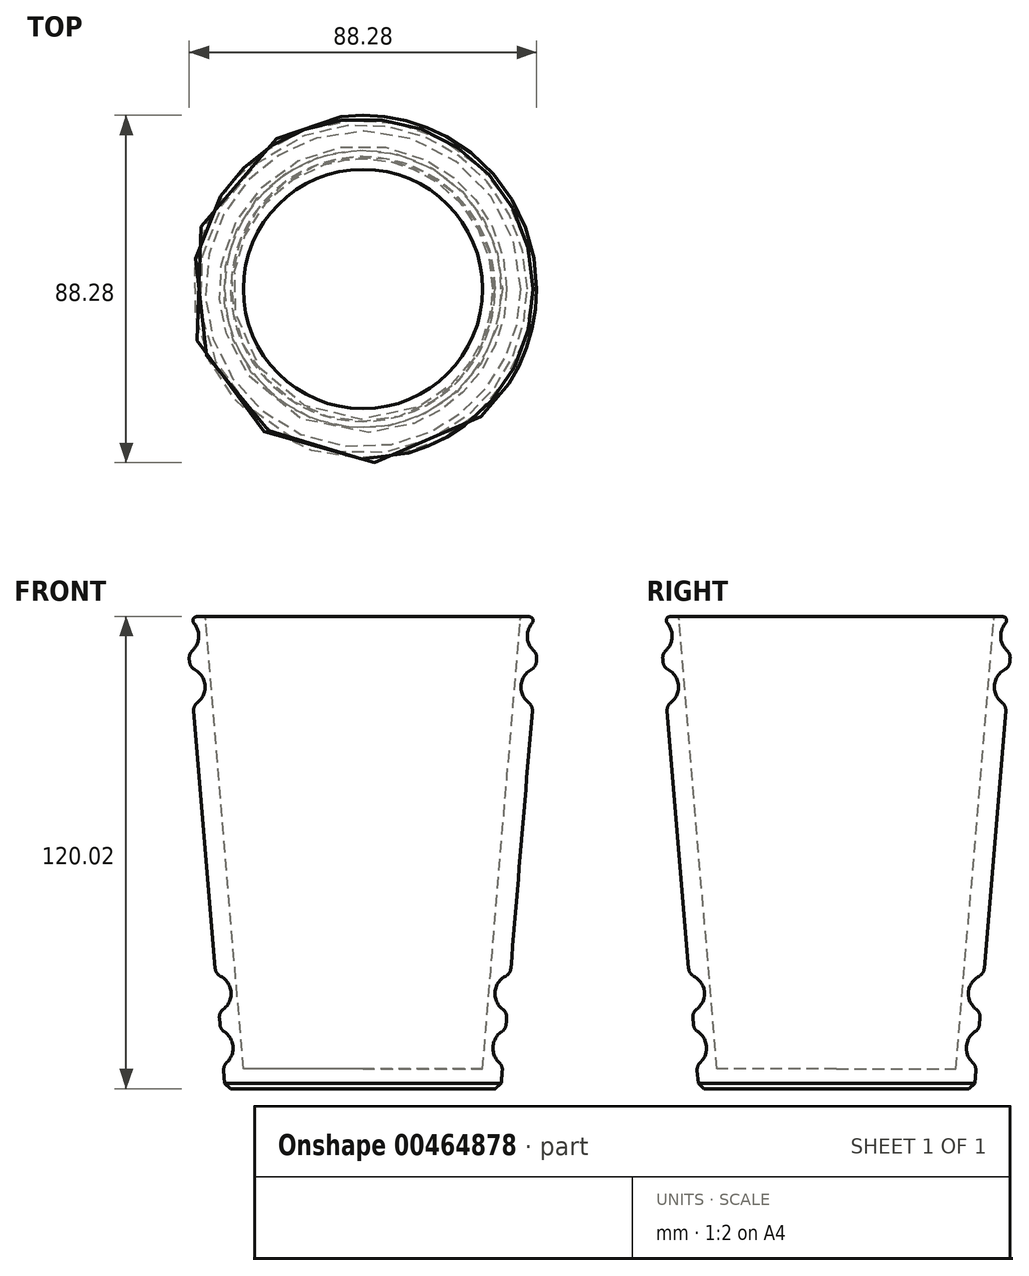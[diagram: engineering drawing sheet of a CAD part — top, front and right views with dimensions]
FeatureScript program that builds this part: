
annotation { "Feature Type Name" : "Feature", "Feature Type Description" : "" }
export const myFeature = defineFeature(function(context is Context, id is Id, definition is map)
    precondition{}
    {
        {
            var Q0;
            Q0=qCreatedBy(makeId("Front.planeOp"),FACE);
            var sketch = newSketch(context, id + "F0", { "sketchPlane" : qUnion([Q0])});
            skLineSegment(sketch, "E0", {"start": v(0, -80.84) * mm, "end": v(-35, -80.84) * mm});
            skLineSegment(sketch, "E1.0", {"start": v(-30.4, -75.84) * mm, "end": v(-40.02, 39.26) * mm});
            skLineSegment(sketch, "E1.1", {"start": v(0, -75.84) * mm, "end": v(-30.4, -75.84) * mm});
            skLineSegment(sketch, "E2", {"start": v(0, -75.84) * mm, "end": v(0, -80.84) * mm});
            skLineSegment(sketch, "E3", {"start": v(-42.35, 39.06) * mm, "end": v(-40.02, 39.26) * mm});
            skArc(sketch, "E4", {"start": v(-44.24, 29.81) * mm, "mid": v(-41.8, 33.34) * mm, "end": v(-43, 37.47) * mm});
            skArc(sketch, "E5", {"start": v(-43.14, 16.63) * mm, "mid": v(-40.14, 21.64) * mm, "end": v(-43.93, 26.08) * mm});
            skArc(sketch, "E6", {"start": v(-35.5, -74.84) * mm, "mid": v(-33.03, -70.1) * mm, "end": v(-36.25, -65.83) * mm});
            skArc(sketch, "E7", {"start": v(-36.63, -61.31) * mm, "mid": v(-33.55, -56.27) * mm, "end": v(-37.43, -51.81) * mm});
            skLineSegment(sketch, "E8", {"start": v(-44.24, 29.81) * mm, "end": v(-43.93, 26.08) * mm});
            skLineSegment(sketch, "E9", {"start": v(-43.14, 16.63) * mm, "end": v(-37.43, -51.81) * mm});
            skLineSegment(sketch, "E10", {"start": v(-36.63, -61.31) * mm, "end": v(-36.25, -65.83) * mm});
            skLineSegment(sketch, "E11", {"start": v(-35.5, -74.84) * mm, "end": v(-35, -80.84) * mm});
            skPoint(sketch, "E12.visualSharp", {"position": v(-45, 38.84) * mm});
            skArc(sketch, "E12.filletArc", {"start": v(-42.35, 39.06) * mm, "mid": v(-43.16, 38.46) * mm, "end": v(-43, 37.47) * mm});
            skSolve(sketch);
        }
        {
            var Q0;
            Q0=makeQuery(id+"F0.imprint","IMPRINT",FACE,{"disambiguationData":[TD([[makeQuery(id+"F0.imprint","IMPRINT",EDGE,{"derivedFrom":sQuery(id+"F0.wireOp",EDGE,"E0")}),-1.0]])]});
            var Q1;
            Q1=sQuery(id+"F0.wireOp",EDGE,"E2");
            revolve(context, id + "F1", {"entities" : qUnion([Q0]), "axis" : qUnion([Q1]), "revolveType" : RevolveType.FULL});
        }
        {
            var Q0;
            Q0=makeQuery(id+"F1.opRevolve","SWEPT_EDGE",EDGE,{"disambiguationData":[OSD([sQuery(id+"F0.wireOp",EDGE,"E1.0"),sQuery(id+"F0.wireOp",EDGE,"E3")])]});
            fillet(context, id + "F2", {"entities" : qUnion([Q0]), "radius" : 1 * mm, "tangentPropagation" : true, "allowEdgeOverflow" : false});
        }
        {
            var Q0;
            Q0=makeQuery(id+"F1.opRevolve","SWEPT_EDGE",EDGE,{"disambiguationData":[OSD([sQuery(id+"F0.wireOp",EDGE,"E4"),sQuery(id+"F0.wireOp",EDGE,"E8")])]});
            var Q1;
            Q1=makeQuery(id+"F1.opRevolve","SWEPT_EDGE",EDGE,{"disambiguationData":[OSD([sQuery(id+"F0.wireOp",EDGE,"E5"),sQuery(id+"F0.wireOp",EDGE,"E8")])]});
            var Q2;
            Q2=makeQuery(id+"F1.opRevolve","SWEPT_EDGE",EDGE,{"disambiguationData":[OSD([sQuery(id+"F0.wireOp",EDGE,"E5"),sQuery(id+"F0.wireOp",EDGE,"E9")])]});
            var Q3;
            Q3=makeQuery(id+"F1.opRevolve","SWEPT_EDGE",EDGE,{"disambiguationData":[OSD([sQuery(id+"F0.wireOp",EDGE,"E7"),sQuery(id+"F0.wireOp",EDGE,"E9")])]});
            var Q4;
            Q4=makeQuery(id+"F1.opRevolve","SWEPT_EDGE",EDGE,{"disambiguationData":[OSD([sQuery(id+"F0.wireOp",EDGE,"E7"),sQuery(id+"F0.wireOp",EDGE,"E10")])]});
            var Q5;
            Q5=makeQuery(id+"F1.opRevolve","SWEPT_EDGE",EDGE,{"disambiguationData":[OSD([sQuery(id+"F0.wireOp",EDGE,"E6"),sQuery(id+"F0.wireOp",EDGE,"E10")])]});
            var Q6;
            Q6=makeQuery(id+"F1.opRevolve","SWEPT_EDGE",EDGE,{"disambiguationData":[OSD([sQuery(id+"F0.wireOp",EDGE,"E6"),sQuery(id+"F0.wireOp",EDGE,"E11")])]});
            fillet(context, id + "F3", {"entities" : qUnion([Q0, Q1, Q2, Q3, Q4, Q5, Q6]), "radius" : 2.5 * mm, "tangentPropagation" : true, "allowEdgeOverflow" : false});
        }
        {
            var Q0;
            Q0=makeQuery(id+"F1.opRevolve","SWEPT_EDGE",EDGE,{"disambiguationData":[OSD([sQuery(id+"F0.wireOp",EDGE,"E0"),sQuery(id+"F0.wireOp",EDGE,"E11")])]});
            chamfer(context, id + "F4", {"entities" : qUnion([Q0]), "width" : 1.5 * mm, "tangentPropagation" : true});
        }
    });
